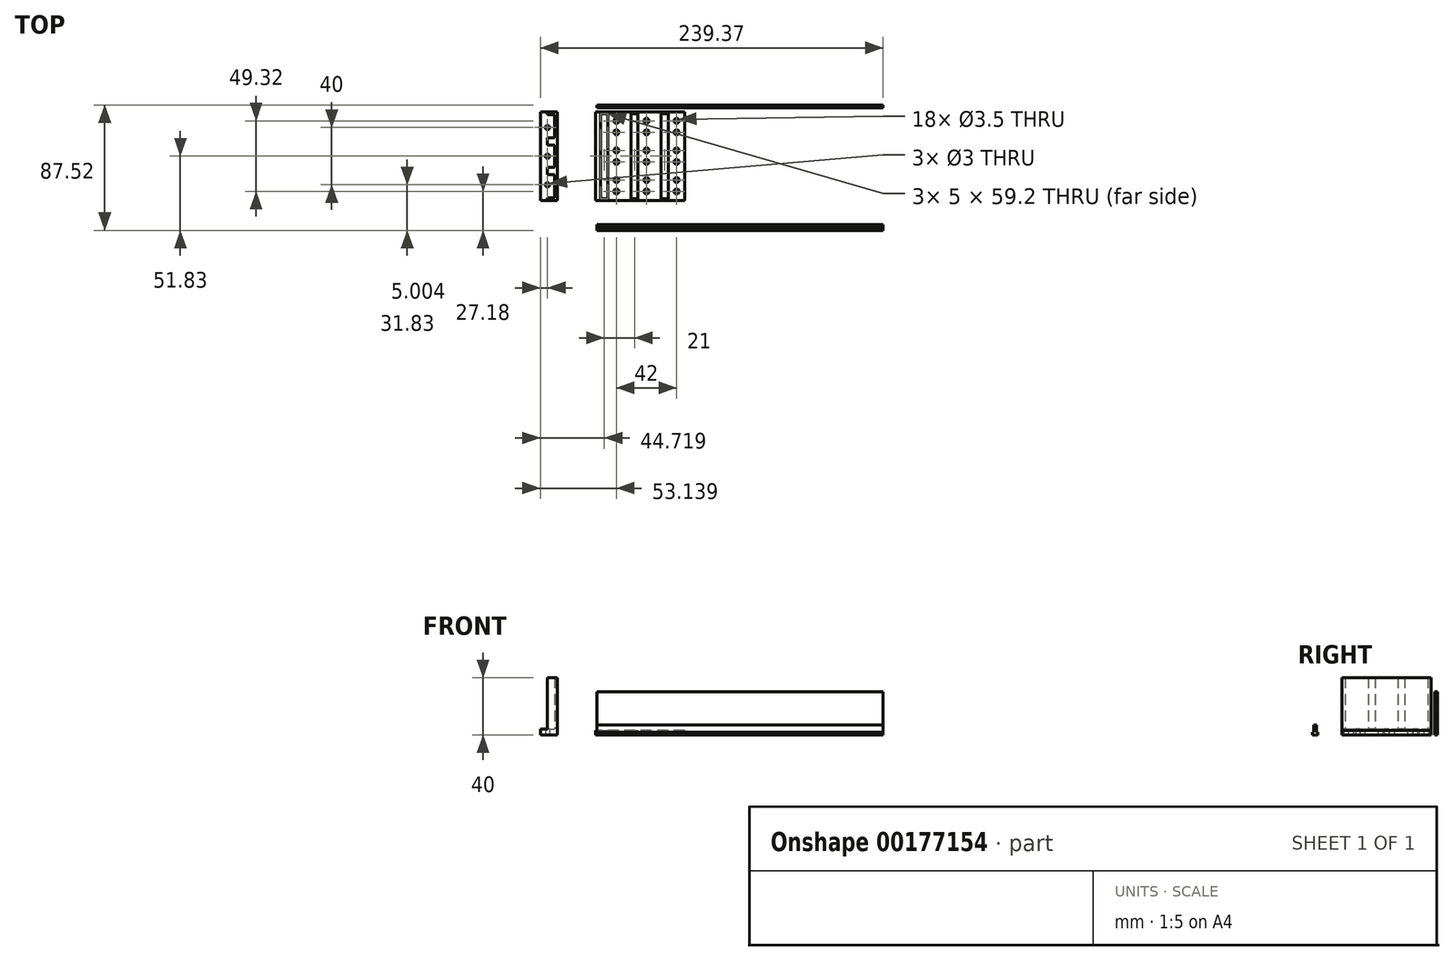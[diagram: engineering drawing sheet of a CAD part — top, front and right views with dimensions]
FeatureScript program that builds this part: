
annotation { "Feature Type Name" : "Feature", "Feature Type Description" : "" }
export const myFeature = defineFeature(function(context is Context, id is Id, definition is map)
    precondition{}
    {
        {
            var Q0;
            Q0=qCreatedBy(makeId("Top.planeOp"),FACE);
            var sketch = newSketch(context, id + "F0", { "sketchPlane" : qUnion([Q0])});
            skLineSegment(sketch, "E0.bottom", {"start": v(-38.73, -31) * mm, "end": v(-100.73, -31) * mm});
            skLineSegment(sketch, "E0.top", {"start": v(-38.73, 31) * mm, "end": v(-100.73, 31) * mm});
            skLineSegment(sketch, "E0.left", {"start": v(-38.73, -31) * mm, "end": v(-38.73, 31) * mm});
            skLineSegment(sketch, "E0.right", {"start": v(-100.73, -31) * mm, "end": v(-100.73, 31) * mm});
            skPoint(sketch, "E0.middle", {"position": v(-69.73, 0) * mm});
            skSolve(sketch);
        }
        {
            var Q0;
            Q0 = qSketchRegion(id + "F0", true);
            extrude(context, id + "F1", {"entities" : qUnion([Q0]), "depth" : 3 * mm});
        }
        {
            var Q0;
            Q0=makeQuery(id+"F1.opExtrude","CAP_FACE",FACE,{"disambiguationData":[OSD([sQuery(id+"F0.wireOp",EDGE,"E0.bottom"),sQuery(id+"F0.wireOp",EDGE,"E0.top"),sQuery(id+"F0.wireOp",EDGE,"E0.left"),sQuery(id+"F0.wireOp",EDGE,"E0.right")])],"isStart":false});
            var sketch = newSketch(context, id + "F2", { "sketchPlane" : qUnion([Q0])});
            skCircle(sketch, "E1", {"center": v(-86.23, 24.67) * mm, "radius": 1.75 * mm});
            skCircle(sketch, "E2", {"center": v(-86.23, 16.67) * mm, "radius": 1.75 * mm});
            skCircle(sketch, "E3.0.1.0", {"center": v(-86.23, 4) * mm, "radius": 1.75 * mm});
            skCircle(sketch, "E3.0.1.1", {"center": v(-86.23, -4) * mm, "radius": 1.75 * mm});
            skCircle(sketch, "E3.0.2.0", {"center": v(-86.23, -16.65) * mm, "radius": 1.75 * mm});
            skCircle(sketch, "E3.0.2.1", {"center": v(-86.23, -24.65) * mm, "radius": 1.75 * mm});
            skCircle(sketch, "E3.1.0.0", {"center": v(-65.23, 24.67) * mm, "radius": 1.75 * mm});
            skCircle(sketch, "E3.1.0.1", {"center": v(-65.23, 16.67) * mm, "radius": 1.75 * mm});
            skCircle(sketch, "E3.1.1.0", {"center": v(-65.23, 4) * mm, "radius": 1.75 * mm});
            skCircle(sketch, "E3.1.1.1", {"center": v(-65.23, -4) * mm, "radius": 1.75 * mm});
            skCircle(sketch, "E3.1.2.0", {"center": v(-65.23, -16.65) * mm, "radius": 1.75 * mm});
            skCircle(sketch, "E3.1.2.1", {"center": v(-65.23, -24.65) * mm, "radius": 1.75 * mm});
            skCircle(sketch, "E3.2.0.0", {"center": v(-44.23, 24.67) * mm, "radius": 1.75 * mm});
            skCircle(sketch, "E3.2.0.1", {"center": v(-44.23, 16.67) * mm, "radius": 1.75 * mm});
            skCircle(sketch, "E3.2.1.0", {"center": v(-44.23, 4) * mm, "radius": 1.75 * mm});
            skCircle(sketch, "E3.2.1.1", {"center": v(-44.23, -4) * mm, "radius": 1.75 * mm});
            skCircle(sketch, "E3.2.2.0", {"center": v(-44.23, -16.65) * mm, "radius": 1.75 * mm});
            skCircle(sketch, "E3.2.2.1", {"center": v(-44.23, -24.65) * mm, "radius": 1.75 * mm});
            skLineSegment(sketch, "E3.direction1", {"start": v(-86.23, 16.67) * mm, "end": v(-65.23, 16.67) * mm, "construction": true});
            skLineSegment(sketch, "E3.direction2", {"start": v(-86.23, 16.67) * mm, "end": v(-86.23, -4) * mm, "construction": true});
            skLineSegment(sketch, "E4.bottom", {"start": v(-97.15, 29.6) * mm, "end": v(-92.15, 29.6) * mm});
            skLineSegment(sketch, "E4.top", {"start": v(-97.15, -29.6) * mm, "end": v(-92.15, -29.6) * mm});
            skLineSegment(sketch, "E4.left", {"start": v(-97.15, 29.6) * mm, "end": v(-97.15, -29.6) * mm});
            skLineSegment(sketch, "E4.right", {"start": v(-92.15, 29.6) * mm, "end": v(-92.15, -29.6) * mm});
            skLineSegment(sketch, "E5.1.0.0", {"start": v(-76.15, -29.6) * mm, "end": v(-71.15, -29.6) * mm});
            skLineSegment(sketch, "E5.1.0.1", {"start": v(-76.15, 29.6) * mm, "end": v(-71.15, 29.6) * mm});
            skLineSegment(sketch, "E5.1.0.2", {"start": v(-76.15, 29.6) * mm, "end": v(-76.15, -29.6) * mm});
            skLineSegment(sketch, "E5.1.0.3", {"start": v(-71.15, 29.6) * mm, "end": v(-71.15, -29.6) * mm});
            skLineSegment(sketch, "E5.2.0.0", {"start": v(-55.15, -29.6) * mm, "end": v(-50.15, -29.6) * mm});
            skLineSegment(sketch, "E5.2.0.1", {"start": v(-55.15, 29.6) * mm, "end": v(-50.15, 29.6) * mm});
            skLineSegment(sketch, "E5.2.0.2", {"start": v(-55.15, 29.6) * mm, "end": v(-55.15, -29.6) * mm});
            skLineSegment(sketch, "E5.2.0.3", {"start": v(-50.15, 29.6) * mm, "end": v(-50.15, -29.6) * mm});
            skLineSegment(sketch, "E5.direction1", {"start": v(-97.15, -29.6) * mm, "end": v(-76.15, -29.6) * mm, "construction": true});
            skSolve(sketch);
        }
        {
            var Q0;
            Q0 = qSketchRegion(id + "F2", true);
            extrude(context, id + "F3", {"entities" : qUnion([Q0]), "operationType" : NewBodyOperationType.REMOVE, "oppositeDirection" : true, "depth" : 25 * mm});
        }
        {
            var Q0;
            Q0=qCreatedBy(makeId("Top.planeOp"),FACE);
            var sketch = newSketch(context, id + "F4", { "sketchPlane" : qUnion([Q0])});
            skLineSegment(sketch, "E6.bottom", {"start": v(-129.37, -31) * mm, "end": v(-139.37, -31) * mm});
            skLineSegment(sketch, "E6.top", {"start": v(-129.37, 31) * mm, "end": v(-139.37, 31) * mm});
            skLineSegment(sketch, "E6.left", {"start": v(-129.37, -31) * mm, "end": v(-129.37, 31) * mm});
            skLineSegment(sketch, "E6.right", {"start": v(-139.37, -31) * mm, "end": v(-139.37, 31) * mm});
            skPoint(sketch, "E6.middle", {"position": v(-134.37, 0) * mm});
            skCircle(sketch, "E7", {"center": v(-134.37, 20) * mm, "radius": 1.5 * mm});
            skCircle(sketch, "E8", {"center": v(-134.37, 0) * mm, "radius": 1.5 * mm});
            skCircle(sketch, "E9", {"center": v(-134.37, -20) * mm, "radius": 1.5 * mm});
            skSolve(sketch);
        }
        {
            var Q0;
            Q0 = qSketchRegion(id + "F4", true);
            extrude(context, id + "F5", {"entities" : qUnion([Q0]), "depth" : 4 * mm});
        }
        {
            var Q0;
            Q0=qCreatedBy(makeId("Top.planeOp"),FACE);
            var sketch = newSketch(context, id + "F6", { "sketchPlane" : qUnion([Q0])});
            skLineSegment(sketch, "E10.bottom", {"start": v(-127.37, -31) * mm, "end": v(-129.37, -31) * mm});
            skLineSegment(sketch, "E10.top", {"start": v(-127.37, 31) * mm, "end": v(-129.37, 31) * mm});
            skLineSegment(sketch, "E10.left", {"start": v(-127.37, -31) * mm, "end": v(-127.37, 31) * mm});
            skLineSegment(sketch, "E10.right", {"start": v(-129.37, -31) * mm, "end": v(-129.37, 31) * mm});
            skPoint(sketch, "E10.middle", {"position": v(-128.37, 0) * mm});
            skLineSegment(sketch, "E11.bottom", {"start": v(-129.37, 31) * mm, "end": v(-134.37, 31) * mm});
            skLineSegment(sketch, "E11.top", {"start": v(-129.37, 29) * mm, "end": v(-134.37, 29) * mm});
            skLineSegment(sketch, "E11.left", {"start": v(-129.37, 31) * mm, "end": v(-129.37, 29) * mm});
            skLineSegment(sketch, "E11.right", {"start": v(-134.37, 31) * mm, "end": v(-134.37, 29) * mm});
            skLineSegment(sketch, "E12.bottom", {"start": v(-129.37, -31) * mm, "end": v(-134.37, -31) * mm});
            skLineSegment(sketch, "E12.top", {"start": v(-129.37, -29) * mm, "end": v(-134.37, -29) * mm});
            skLineSegment(sketch, "E12.left", {"start": v(-129.37, -31) * mm, "end": v(-129.37, -29) * mm});
            skLineSegment(sketch, "E12.right", {"start": v(-134.37, -31) * mm, "end": v(-134.37, -29) * mm});
            skLineSegment(sketch, "E13.bottom", {"start": v(-129.37, 7.84) * mm, "end": v(-134.37, 7.84) * mm});
            skLineSegment(sketch, "E13.top", {"start": v(-129.37, 12.84) * mm, "end": v(-134.37, 12.84) * mm});
            skLineSegment(sketch, "E13.left", {"start": v(-129.37, 7.84) * mm, "end": v(-129.37, 12.84) * mm});
            skLineSegment(sketch, "E13.right", {"start": v(-134.37, 7.84) * mm, "end": v(-134.37, 12.84) * mm});
            skPoint(sketch, "E13.middle", {"position": v(-131.87, 10.34) * mm});
            skLineSegment(sketch, "E14.bottom", {"start": v(-129.37, -12.82) * mm, "end": v(-134.37, -12.82) * mm});
            skLineSegment(sketch, "E14.top", {"start": v(-129.37, -7.82) * mm, "end": v(-134.37, -7.82) * mm});
            skLineSegment(sketch, "E14.left", {"start": v(-129.37, -12.82) * mm, "end": v(-129.37, -7.82) * mm});
            skLineSegment(sketch, "E14.right", {"start": v(-134.37, -12.82) * mm, "end": v(-134.37, -7.82) * mm});
            skPoint(sketch, "E14.middle", {"position": v(-131.87, -10.32) * mm});
            skSolve(sketch);
        }
        {
            var Q0;
            Q0 = qSketchRegion(id + "F6", true);
            extrude(context, id + "F7", {"entities" : qUnion([Q0]), "operationType" : NewBodyOperationType.ADD, "depth" : 40 * mm});
        }
        {
            var Q0;
            Q0=qCreatedBy(makeId("Top.planeOp"),FACE);
            var sketch = newSketch(context, id + "F8", { "sketchPlane" : qUnion([Q0])});
            skLineSegment(sketch, "E15.bottom", {"start": v(100, 33.69) * mm, "end": v(-100, 33.69) * mm});
            skLineSegment(sketch, "E15.top", {"start": v(100, 35.69) * mm, "end": v(-100, 35.69) * mm});
            skLineSegment(sketch, "E15.left", {"start": v(100, 33.69) * mm, "end": v(100, 35.69) * mm});
            skLineSegment(sketch, "E15.right", {"start": v(-100, 33.69) * mm, "end": v(-100, 35.69) * mm});
            skPoint(sketch, "E15.middle", {"position": v(0, 34.69) * mm});
            skSolve(sketch);
        }
        {
            var Q0;
            Q0 = qSketchRegion(id + "F8", true);
            extrude(context, id + "F9", {"entities" : qUnion([Q0]), "depth" : 30 * mm});
        }
        {
            var Q0;
            Q0=qCreatedBy(makeId("Top.planeOp"),FACE);
            var sketch = newSketch(context, id + "F10", { "sketchPlane" : qUnion([Q0])});
            skLineSegment(sketch, "E16.bottom", {"start": v(100, -47.83) * mm, "end": v(-100, -47.83) * mm});
            skLineSegment(sketch, "E16.top", {"start": v(100, -51.83) * mm, "end": v(-100, -51.83) * mm});
            skLineSegment(sketch, "E16.left", {"start": v(100, -47.83) * mm, "end": v(100, -51.83) * mm});
            skLineSegment(sketch, "E16.right", {"start": v(-100, -47.83) * mm, "end": v(-100, -51.83) * mm});
            skPoint(sketch, "E16.middle", {"position": v(0, -49.83) * mm});
            skSolve(sketch);
        }
        {
            var Q0;
            Q0 = qSketchRegion(id + "F10", true);
            extrude(context, id + "F11", {"entities" : qUnion([Q0]), "depth" : 2 * mm});
        }
        {
            var Q0;
            Q0=makeQuery(id+"F11.opExtrude","CAP_FACE",FACE,{"disambiguationData":[OSD([sQuery(id+"F10.wireOp",EDGE,"E16.bottom"),sQuery(id+"F10.wireOp",EDGE,"E16.top"),sQuery(id+"F10.wireOp",EDGE,"E16.left"),sQuery(id+"F10.wireOp",EDGE,"E16.right")])],"isStart":false});
            var sketch = newSketch(context, id + "F12", { "sketchPlane" : qUnion([Q0])});
            skLineSegment(sketch, "E17.bottom", {"start": v(100, -50.83) * mm, "end": v(-100, -50.83) * mm});
            skLineSegment(sketch, "E17.top", {"start": v(100, -48.83) * mm, "end": v(-100, -48.83) * mm});
            skLineSegment(sketch, "E17.left", {"start": v(100, -50.83) * mm, "end": v(100, -48.83) * mm});
            skLineSegment(sketch, "E17.right", {"start": v(-100, -50.83) * mm, "end": v(-100, -48.83) * mm});
            skPoint(sketch, "E17.middle", {"position": v(0, -49.83) * mm});
            skSolve(sketch);
        }
        {
            var Q0;
            Q0 = qSketchRegion(id + "F12", true);
            extrude(context, id + "F13", {"entities" : qUnion([Q0]), "operationType" : NewBodyOperationType.ADD, "depth" : 5 * mm});
        }
    });
